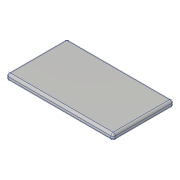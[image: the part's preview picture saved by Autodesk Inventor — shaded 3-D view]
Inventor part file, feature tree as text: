
AUTODESK INVENTOR PART (.ipt)
format: ipt  version: 2017 (Build 210142000, 142)  size: 109,568 bytes
history: native  units: in
note: dims shown in document units (in); Inventor stores cm internally (conversion verified against a paired STEP export)
features: sketch x2, extrude x1, fillet x1
ambient origin geometry x8: Origin, YZ Plane, XZ Plane, XY Plane, X Axis, Y Axis, Z Axis, Center Point
bodies: Solid1 (feature_tree)
feature tree (4):
  extrude  "Extrusion1"  Depth=1.42in
  sketch  "Sketch2"  dims[d4=0.05in]
  fillet  "Fillet1"  Radius=0.15in
  sketch  "Sketch1"  dims[d0=2.5in d1=1.42in d2=0.15in d3=0.0in]
